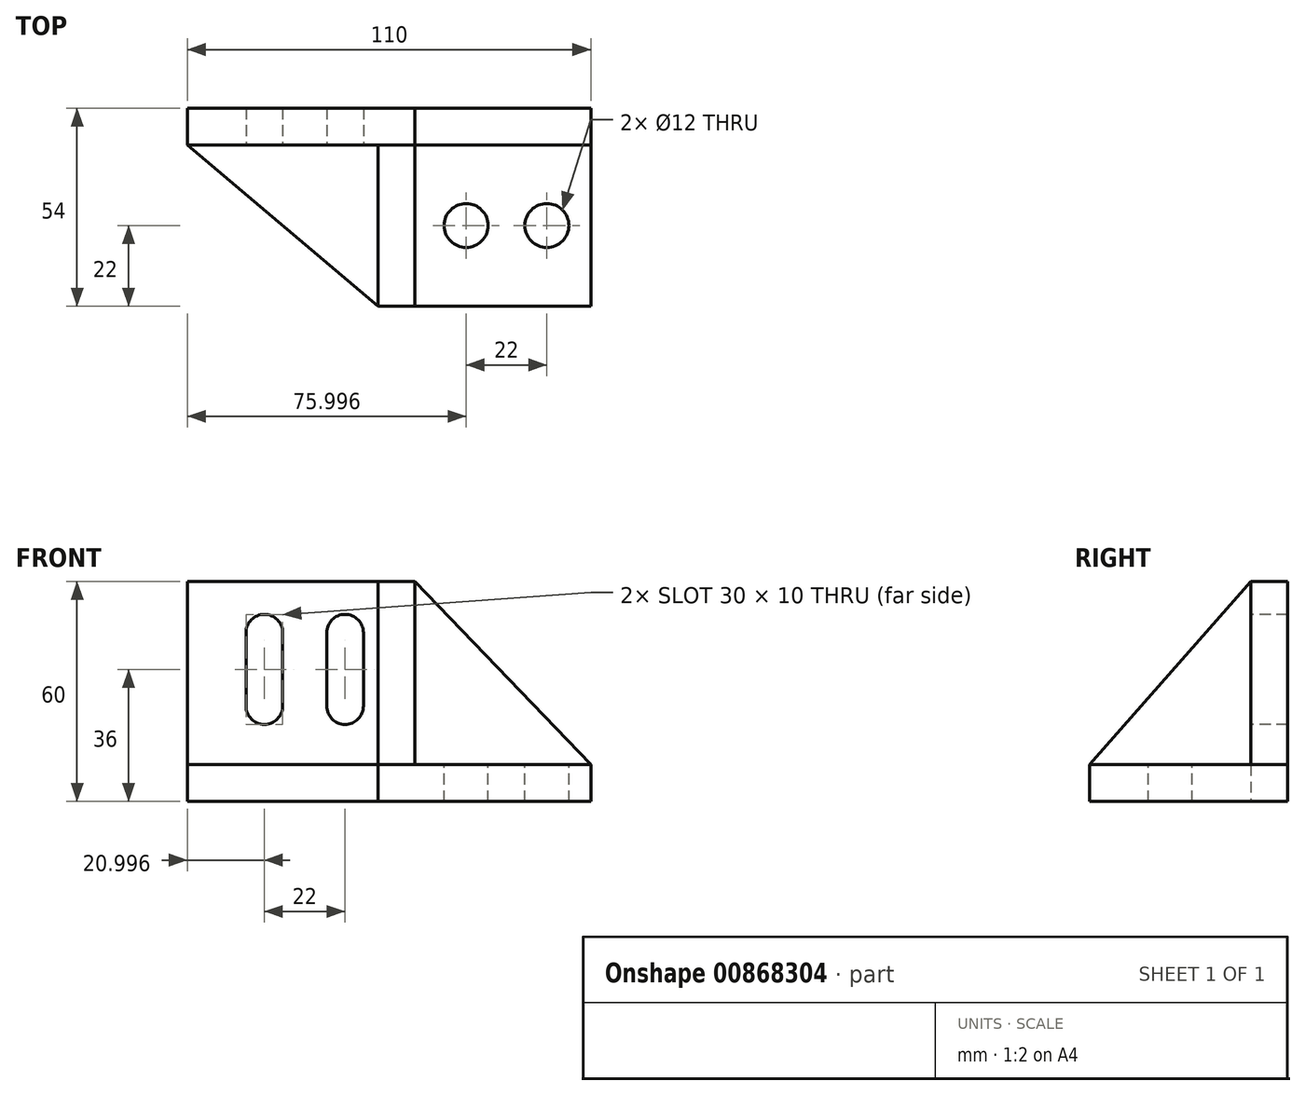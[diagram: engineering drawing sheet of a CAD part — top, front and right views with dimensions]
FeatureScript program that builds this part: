
annotation { "Feature Type Name" : "Feature", "Feature Type Description" : "" }
export const myFeature = defineFeature(function(context is Context, id is Id, definition is map)
    precondition{}
    {
        {
            var Q0;
            Q0=qCreatedBy(makeId("Top.planeOp"),FACE);
            var sketch = newSketch(context, id + "F0", { "sketchPlane" : qUnion([Q0])});
            skLineSegment(sketch, "E0", {"start": v(-27.5, 0) * mm, "end": v(82.5, 0) * mm});
            skLineSegment(sketch, "E1", {"start": v(82.5, 0) * mm, "end": v(82.5, -54) * mm});
            skLineSegment(sketch, "E2", {"start": v(82.5, -54) * mm, "end": v(24.5, -54) * mm});
            skLineSegment(sketch, "E3", {"start": v(24.5, -54) * mm, "end": v(-27.5, -10) * mm});
            skLineSegment(sketch, "E4", {"start": v(24.5, -54) * mm, "end": v(24.5, -10) * mm});
            skLineSegment(sketch, "E5", {"start": v(24.5, -10) * mm, "end": v(82.5, -10) * mm});
            skLineSegment(sketch, "E6", {"start": v(82.5, -10) * mm, "end": v(24.5, -10) * mm});
            skLineSegment(sketch, "E7", {"start": v(-27.5, -10) * mm, "end": v(-27.5, 0) * mm});
            skLineSegment(sketch, "E8", {"start": v(-27.5, -10) * mm, "end": v(24.5, -10) * mm});
            skLineSegment(sketch, "E9", {"start": v(34.5, -54) * mm, "end": v(34.5, -10) * mm});
            skLineSegment(sketch, "E10", {"start": v(34.5, -10) * mm, "end": v(24.5, -10) * mm});
            skSolve(sketch);
        }
        {
            var Q0;
            {var subQ5=sQuery(id+"F0.wireOp",EDGE,"E0");Q0=makeQuery(id+"F0.imprint","IMPRINT",FACE,{"disambiguationData":[TD([[makeQuery(id+"F0.imprint","IMPRINT",EDGE,{"derivedFrom":subQ5}),-1.0]])]});}
            var Q1;
            {var subQ0=sQuery(id+"F0.wireOp",EDGE,"E4");Q1=makeQuery(id+"F0.imprint","IMPRINT",FACE,{"disambiguationData":[TD([[makeQuery(id+"F0.imprint","IMPRINT",EDGE,{"derivedFrom":subQ0}),-1.0]])]});}
            extrude(context, id + "F1", {"entities" : qUnion([Q0, Q1]), "depth" : 60 * mm, "offsetDistance" : 25 * mm});
        }
        {
            var Q0;
            Q0=makeQuery(id+"F0.imprint","IMPRINT",FACE,{"disambiguationData":[TD([[makeQuery(id+"F0.imprint","IMPRINT",EDGE,{"derivedFrom":sQuery(id+"F0.wireOp",EDGE,"E3")}),-1.0]])]});
            var Q1;
            {var subQ5=sQuery(id+"F0.wireOp",EDGE,"E9");Q1=makeQuery(id+"F0.imprint","IMPRINT",FACE,{"disambiguationData":[TD([[makeQuery(id+"F0.imprint","IMPRINT",EDGE,{"derivedFrom":subQ5}),-1.0]])]});}
            extrude(context, id + "F2", {"entities" : qUnion([Q0, Q1]), "operationType" : NewBodyOperationType.ADD, "depth" : 10 * mm, "offsetDistance" : 25 * mm});
        }
        {
            var Q0;
            Q0=makeQuery(id+"F1.opExtrude","SWEPT_FACE",FACE,{"disambiguationData":[OSD([sQuery(id+"F0.wireOp",EDGE,"E9")])]});
            var sketch = newSketch(context, id + "F3", { "sketchPlane" : qUnion([Q0])});
            skLineSegment(sketch, "E11", {"start": v(-54, 10) * mm, "end": v(-10, 60) * mm});
            skSolve(sketch);
        }
        {
            var Q0;
            Q0=makeQuery(id+"F3.imprint","IMPRINT",FACE,{"disambiguationData":[TD([[makeQuery(id+"F3.imprint","IMPRINT",EDGE,{"derivedFrom":sQuery(id+"F3.wireOp",EDGE,"E11")}),1.0]])]});
            extrude(context, id + "F4", {"entities" : qUnion([Q0]), "operationType" : NewBodyOperationType.REMOVE, "oppositeDirection" : true, "depth" : 25 * mm, "offsetDistance" : 25 * mm});
        }
        {
            var Q0;
            Q0=makeQuery(id+"F1.opExtrude","SWEPT_FACE",FACE,{"disambiguationData":[OSD([sQuery(id+"F0.wireOp",EDGE,"E5")])]});
            var sketch = newSketch(context, id + "F5", { "sketchPlane" : qUnion([Q0])});
            skLineSegment(sketch, "E12", {"start": v(34.5, 60) * mm, "end": v(82.5, 10) * mm});
            skSolve(sketch);
        }
        {
            var Q0;
            Q0=makeQuery(id+"F5.imprint","IMPRINT",FACE,{"disambiguationData":[TD([[makeQuery(id+"F5.imprint","IMPRINT",EDGE,{"derivedFrom":sQuery(id+"F5.wireOp",EDGE,"E12")}),1.0]])]});
            extrude(context, id + "F6", {"entities" : qUnion([Q0]), "operationType" : NewBodyOperationType.REMOVE, "oppositeDirection" : true, "depth" : 25 * mm, "offsetDistance" : 25 * mm});
        }
        {
            var Q0;
            Q0=makeQuery(id+"F2.opExtrude","CAP_FACE",FACE,{"disambiguationData":[OSD([sQuery(id+"F0.wireOp",EDGE,"E1"),sQuery(id+"F0.wireOp",EDGE,"E2"),sQuery(id+"F0.wireOp",EDGE,"E5"),sQuery(id+"F0.wireOp",EDGE,"E9")])],"isStart":false});
            var sketch = newSketch(context, id + "F7", { "sketchPlane" : qUnion([Q0])});
            skCircle(sketch, "E13", {"center": v(48.5, -32) * mm, "radius": 6 * mm});
            skCircle(sketch, "E14", {"center": v(70.5, -32) * mm, "radius": 6 * mm});
            skPoint(sketch, "E15.orphan", {"position": v(58.5, -10) * mm});
            skPoint(sketch, "E16.end.orphan", {"position": v(58.5, -54) * mm});
            skLineSegment(sketch, "E17.trimOffspring", {"start": v(76.5, -32) * mm, "end": v(82.5, -32) * mm});
            skPoint(sketch, "E18.start.orphan", {"position": v(34.5, -32) * mm});
            skSolve(sketch);
        }
        {
            var Q0;
            Q0 = qSketchRegion(id + "F7", true);
            extrude(context, id + "F8", {"entities" : qUnion([Q0]), "operationType" : NewBodyOperationType.REMOVE, "endBound" : BoundingType.THROUGH_ALL, "oppositeDirection" : true, "depth" : 25 * mm, "offsetDistance" : 25 * mm});
        }
        {
            var Q0;
            Q0=makeQuery(id+"F1.opExtrude","SWEPT_FACE",FACE,{"disambiguationData":[OSD([sQuery(id+"F0.wireOp",EDGE,"E8")])]});
            var sketch = newSketch(context, id + "F9", { "sketchPlane" : qUnion([Q0])});
            skLineSegment(sketch, "E19", {"start": v(-11.5, 46) * mm, "end": v(-11.5, 26) * mm});
            skArc(sketch, "E20", {"start": v(-1.5, 46) * mm, "mid": v(-6.5, 51) * mm, "end": v(-11.5, 46) * mm});
            skLineSegment(sketch, "E21", {"start": v(-1.5, 46) * mm, "end": v(-1.5, 26) * mm});
            skArc(sketch, "E22", {"start": v(-11.5, 26) * mm, "mid": v(-6.5, 21) * mm, "end": v(-1.5, 26) * mm});
            skLineSegment(sketch, "E23", {"start": v(10.5, 46) * mm, "end": v(10.5, 26) * mm});
            skArc(sketch, "E24", {"start": v(20.5, 46) * mm, "mid": v(15.5, 51) * mm, "end": v(10.5, 46) * mm});
            skLineSegment(sketch, "E25", {"start": v(20.5, 46) * mm, "end": v(20.5, 26) * mm});
            skArc(sketch, "E26", {"start": v(10.5, 26) * mm, "mid": v(15.5, 21) * mm, "end": v(20.5, 26) * mm});
            skSolve(sketch);
        }
        {
            var Q0;
            Q0=makeQuery(id+"F9.imprint","IMPRINT",FACE,{"disambiguationData":[TD([[makeQuery(id+"F9.imprint","IMPRINT",EDGE,{"derivedFrom":sQuery(id+"F9.wireOp",EDGE,"E19")}),1.0]])]});
            var Q1;
            Q1=makeQuery(id+"F9.imprint","IMPRINT",FACE,{"disambiguationData":[TD([[makeQuery(id+"F9.imprint","IMPRINT",EDGE,{"derivedFrom":sQuery(id+"F9.wireOp",EDGE,"E23")}),1.0]])]});
            extrude(context, id + "F10", {"entities" : qUnion([Q0, Q1]), "operationType" : NewBodyOperationType.REMOVE, "endBound" : BoundingType.THROUGH_ALL, "oppositeDirection" : true, "depth" : 25 * mm, "offsetDistance" : 25 * mm});
        }
    });
